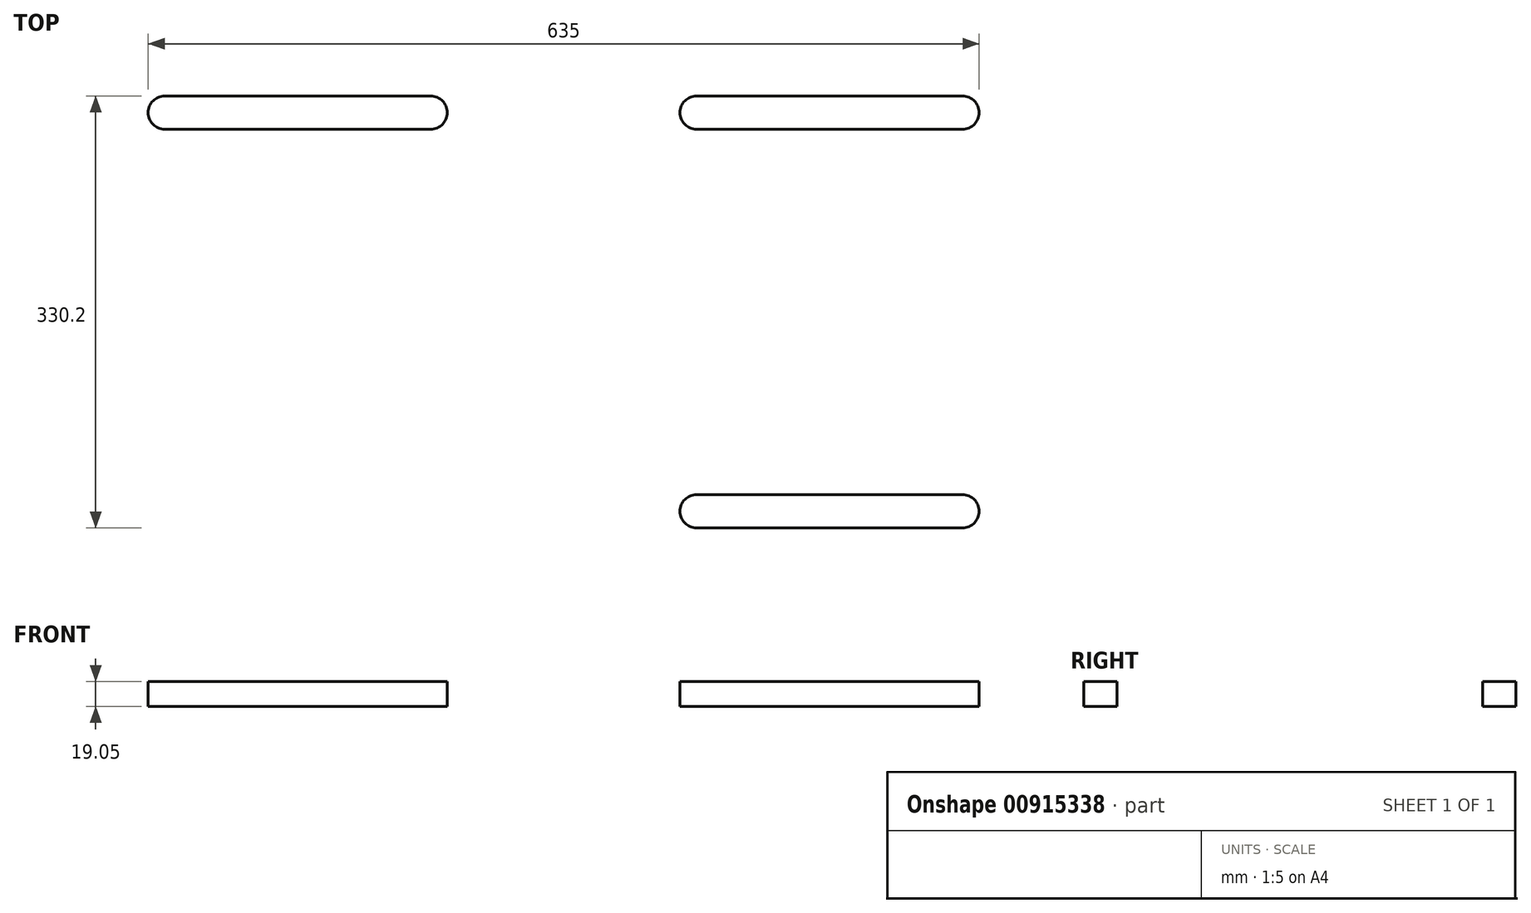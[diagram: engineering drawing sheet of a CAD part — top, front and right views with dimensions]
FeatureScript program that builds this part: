
annotation { "Feature Type Name" : "Feature", "Feature Type Description" : "" }
export const myFeature = defineFeature(function(context is Context, id is Id, definition is map)
    precondition{}
    {
        {
            var Q0;
            Q0=qCreatedBy(makeId("Top.planeOp"),FACE);
            var sketch = newSketch(context, id + "F0", { "sketchPlane" : qUnion([Q0])});
            skLineSegment(sketch, "E0.bottom", {"start": v(0, 0) * mm, "end": v(889, 0) * mm});
            skLineSegment(sketch, "E0.top", {"start": v(0, 596.9) * mm, "end": v(889, 596.9) * mm});
            skLineSegment(sketch, "E0.left", {"start": v(0, 0) * mm, "end": v(0, 596.9) * mm});
            skLineSegment(sketch, "E0.right", {"start": v(889, 0) * mm, "end": v(889, 596.9) * mm});
            skSolve(sketch);
        }
        {
            var Q0;
            Q0 = qSketchRegion(id + "F0", true);
            extrude(context, id + "F1", {"entities" : qUnion([Q0]), "depth" : 19.05 * mm, "offsetDistance" : 25.4 * mm});
        }
        {
            var Q0;
            Q0=makeQuery(id+"F1.opExtrude","CAP_FACE",FACE,{"disambiguationData":[OSD([sQuery(id+"F0.wireOp",EDGE,"E0.bottom"),sQuery(id+"F0.wireOp",EDGE,"E0.top"),sQuery(id+"F0.wireOp",EDGE,"E0.left"),sQuery(id+"F0.wireOp",EDGE,"E0.right")])],"isStart":false});
            var sketch = newSketch(context, id + "F2", { "sketchPlane" : qUnion([Q0])});
            skLineSegment(sketch, "E1", {"start": v(444.5, 596.9) * mm, "end": v(444.5, 0) * mm, "construction": true});
            skLineSegment(sketch, "E2", {"start": v(0, 298.45) * mm, "end": v(889, 298.45) * mm, "construction": true});
            skArc(sketch, "E3", {"start": v(139.7, 311.15) * mm, "mid": v(127, 298.45) * mm, "end": v(139.7, 285.75) * mm});
            skLineSegment(sketch, "E4.0", {"start": v(241.3, 596.9) * mm, "end": v(241.3, 0) * mm, "construction": true});
            skLineSegment(sketch, "E5.0", {"start": v(647.7, 596.9) * mm, "end": v(647.7, 0) * mm, "construction": true});
            skArc(sketch, "E6.MirrorC", {"start": v(342.9, 311.15) * mm, "mid": v(355.6, 298.45) * mm, "end": v(342.9, 285.75) * mm});
            skLineSegment(sketch, "E7", {"start": v(139.7, 285.75) * mm, "end": v(342.9, 285.75) * mm});
            skLineSegment(sketch, "E8", {"start": v(139.7, 311.15) * mm, "end": v(342.9, 311.15) * mm});
            skArc(sketch, "E9.MirrorCS", {"start": v(546.1, 311.15) * mm, "mid": v(533.4, 298.45) * mm, "end": v(546.1, 285.75) * mm});
            skArc(sketch, "E10.MirrorCS", {"start": v(749.3, 311.15) * mm, "mid": v(762, 298.45) * mm, "end": v(749.3, 285.75) * mm});
            skLineSegment(sketch, "E11.MirrorCS", {"start": v(749.3, 311.15) * mm, "end": v(546.1, 311.15) * mm});
            skLineSegment(sketch, "E12.MirrorCS", {"start": v(749.3, 285.75) * mm, "end": v(546.1, 285.75) * mm});
            skLineSegment(sketch, "E13.0.1.0", {"start": v(139.7, 438.15) * mm, "end": v(342.9, 438.15) * mm});
            skArc(sketch, "E13.0.1.1", {"start": v(342.9, 463.55) * mm, "mid": v(355.6, 450.85) * mm, "end": v(342.9, 438.15) * mm});
            skArc(sketch, "E13.0.1.2", {"start": v(749.3, 463.55) * mm, "mid": v(762, 450.85) * mm, "end": v(749.3, 438.15) * mm});
            skArc(sketch, "E13.0.1.3", {"start": v(546.1, 463.55) * mm, "mid": v(533.4, 450.85) * mm, "end": v(546.1, 438.15) * mm});
            skLineSegment(sketch, "E13.0.1.4", {"start": v(749.3, 438.15) * mm, "end": v(546.1, 438.15) * mm});
            skArc(sketch, "E13.0.1.5", {"start": v(139.7, 463.55) * mm, "mid": v(127, 450.85) * mm, "end": v(139.7, 438.15) * mm});
            skLineSegment(sketch, "E13.0.1.6", {"start": v(139.7, 463.55) * mm, "end": v(342.9, 463.55) * mm});
            skLineSegment(sketch, "E13.0.1.7", {"start": v(749.3, 463.55) * mm, "end": v(546.1, 463.55) * mm});
            skArc(sketch, "E13.0.1.8", {"start": v(139.7, 463.55) * mm, "mid": v(127, 450.85) * mm, "end": v(139.7, 438.15) * mm});
            skLineSegment(sketch, "E13.0.1.9", {"start": v(749.3, 463.55) * mm, "end": v(546.1, 463.55) * mm});
            skLineSegment(sketch, "E13.0.1.10", {"start": v(139.7, 463.55) * mm, "end": v(342.9, 463.55) * mm});
            skArc(sketch, "E13.0.1.11", {"start": v(749.3, 463.55) * mm, "mid": v(762, 450.85) * mm, "end": v(749.3, 438.15) * mm});
            skLineSegment(sketch, "E13.0.1.12", {"start": v(139.7, 438.15) * mm, "end": v(342.9, 438.15) * mm});
            skLineSegment(sketch, "E13.0.1.13", {"start": v(749.3, 438.15) * mm, "end": v(546.1, 438.15) * mm});
            skArc(sketch, "E13.0.1.14", {"start": v(546.1, 463.55) * mm, "mid": v(533.4, 450.85) * mm, "end": v(546.1, 438.15) * mm});
            skArc(sketch, "E13.0.1.15", {"start": v(342.9, 463.55) * mm, "mid": v(355.6, 450.85) * mm, "end": v(342.9, 438.15) * mm});
            skArc(sketch, "E13.0.1.16", {"start": v(749.3, 463.55) * mm, "mid": v(762, 450.85) * mm, "end": v(749.3, 438.15) * mm});
            skArc(sketch, "E13.0.1.17", {"start": v(546.1, 463.55) * mm, "mid": v(533.4, 450.85) * mm, "end": v(546.1, 438.15) * mm});
            skLineSegment(sketch, "E13.0.1.18", {"start": v(749.3, 438.15) * mm, "end": v(546.1, 438.15) * mm});
            skLineSegment(sketch, "E13.0.1.19", {"start": v(749.3, 463.55) * mm, "end": v(546.1, 463.55) * mm});
            skArc(sketch, "E13.0.1.20", {"start": v(546.1, 463.55) * mm, "mid": v(533.4, 450.85) * mm, "end": v(546.1, 438.15) * mm});
            skLineSegment(sketch, "E13.0.1.21", {"start": v(749.3, 438.15) * mm, "end": v(546.1, 438.15) * mm});
            skLineSegment(sketch, "E13.0.1.22", {"start": v(749.3, 463.55) * mm, "end": v(546.1, 463.55) * mm});
            skArc(sketch, "E13.0.1.23", {"start": v(749.3, 463.55) * mm, "mid": v(762, 450.85) * mm, "end": v(749.3, 438.15) * mm});
            skLineSegment(sketch, "E13.direction1", {"start": v(139.7, 285.75) * mm, "end": v(165.1, 285.75) * mm, "construction": true});
            skLineSegment(sketch, "E13.direction2", {"start": v(139.7, 285.75) * mm, "end": v(139.7, 438.15) * mm, "construction": true});
            skArc(sketch, "E14.MirrorCS", {"start": v(546.1, 133.35) * mm, "mid": v(533.4, 146.05) * mm, "end": v(546.1, 158.75) * mm});
            skLineSegment(sketch, "E15.MirrorCS", {"start": v(749.3, 158.75) * mm, "end": v(546.1, 158.75) * mm});
            skArc(sketch, "E16.MirrorCS", {"start": v(749.3, 133.35) * mm, "mid": v(762, 146.05) * mm, "end": v(749.3, 158.75) * mm});
            skLineSegment(sketch, "E17.MirrorCS", {"start": v(749.3, 133.35) * mm, "end": v(546.1, 133.35) * mm});
            skArc(sketch, "E18.MirrorCS", {"start": v(342.9, 133.35) * mm, "mid": v(355.6, 146.05) * mm, "end": v(342.9, 158.75) * mm});
            skLineSegment(sketch, "E19.MirrorCS", {"start": v(139.7, 133.35) * mm, "end": v(342.9, 133.35) * mm});
            skArc(sketch, "E20.MirrorCS", {"start": v(139.7, 133.35) * mm, "mid": v(127, 146.05) * mm, "end": v(139.7, 158.75) * mm});
            skLineSegment(sketch, "E21.MirrorCS", {"start": v(139.7, 158.75) * mm, "end": v(342.9, 158.75) * mm});
            skSolve(sketch);
        }
        {
            var Q0;
            Q0=makeQuery(id+"F2.imprint","IMPRINT",FACE,{"disambiguationData":[TD([[makeQuery(id+"F2.imprint","IMPRINT",EDGE,{"derivedFrom":sQuery(id+"F2.wireOp",EDGE,"E8")}),1.0]])]});
            var sketch = newSketch(context, id + "F3", { "sketchPlane" : qUnion([Q0])});
            skCircle(sketch, "E22", {"center": v(38.1, 558.8) * mm, "radius": 12.7 * mm});
            skCircle(sketch, "E23.1.0.0", {"center": v(139.7, 558.8) * mm, "radius": 12.7 * mm});
            skCircle(sketch, "E23.2.0.0", {"center": v(241.3, 558.8) * mm, "radius": 12.7 * mm});
            skCircle(sketch, "E23.3.0.0", {"center": v(342.9, 558.8) * mm, "radius": 12.7 * mm});
            skCircle(sketch, "E23.4.0.0", {"center": v(444.5, 558.8) * mm, "radius": 12.7 * mm});
            skCircle(sketch, "E23.5.0.0", {"center": v(546.1, 558.8) * mm, "radius": 12.7 * mm});
            skCircle(sketch, "E23.6.0.0", {"center": v(647.7, 558.8) * mm, "radius": 12.7 * mm});
            skCircle(sketch, "E23.7.0.0", {"center": v(749.3, 558.8) * mm, "radius": 12.7 * mm});
            skCircle(sketch, "E23.8.0.0", {"center": v(850.9, 558.8) * mm, "radius": 12.7 * mm});
            skLineSegment(sketch, "E23.direction1", {"start": v(38.1, 558.8) * mm, "end": v(139.7, 558.8) * mm, "construction": true});
            skCircle(sketch, "E24.MirrorC", {"center": v(342.9, 38.1) * mm, "radius": 12.7 * mm});
            skCircle(sketch, "E25.MirrorC", {"center": v(850.9, 38.1) * mm, "radius": 12.7 * mm});
            skCircle(sketch, "E26.MirrorC", {"center": v(139.7, 38.1) * mm, "radius": 12.7 * mm});
            skCircle(sketch, "E27.MirrorC", {"center": v(241.3, 38.1) * mm, "radius": 12.7 * mm});
            skCircle(sketch, "E28.MirrorC", {"center": v(647.7, 38.1) * mm, "radius": 12.7 * mm});
            skCircle(sketch, "E29.MirrorC", {"center": v(749.3, 38.1) * mm, "radius": 12.7 * mm});
            skCircle(sketch, "E30.MirrorC", {"center": v(38.1, 38.1) * mm, "radius": 12.7 * mm});
            skCircle(sketch, "E31.MirrorC", {"center": v(444.5, 38.1) * mm, "radius": 12.7 * mm});
            skCircle(sketch, "E32.MirrorC", {"center": v(546.1, 38.1) * mm, "radius": 12.7 * mm});
            skLineSegment(sketch, "E33.MirrorCS", {"start": v(38.1, 38.1) * mm, "end": v(139.7, 38.1) * mm, "construction": true});
            skCircle(sketch, "E34.0.1.0", {"center": v(38.1, 457.2) * mm, "radius": 12.7 * mm});
            skCircle(sketch, "E34.0.1.1", {"center": v(38.1, 457.2) * mm, "radius": 12.7 * mm});
            skCircle(sketch, "E34.0.2.0", {"center": v(38.1, 355.6) * mm, "radius": 12.7 * mm});
            skCircle(sketch, "E34.0.2.1", {"center": v(38.1, 355.6) * mm, "radius": 12.7 * mm});
            skCircle(sketch, "E34.0.3.0", {"center": v(38.1, 254) * mm, "radius": 12.7 * mm});
            skCircle(sketch, "E34.0.3.1", {"center": v(38.1, 254) * mm, "radius": 12.7 * mm});
            skCircle(sketch, "E34.0.4.0", {"center": v(38.1, 152.4) * mm, "radius": 12.7 * mm});
            skCircle(sketch, "E34.0.4.1", {"center": v(38.1, 152.4) * mm, "radius": 12.7 * mm});
            skLineSegment(sketch, "E34.direction1", {"start": v(38.1, 558.8) * mm, "end": v(63.5, 558.8) * mm, "construction": true});
            skLineSegment(sketch, "E34.direction2", {"start": v(38.1, 558.8) * mm, "end": v(38.1, 457.2) * mm, "construction": true});
            skCircle(sketch, "E35.MirrorC", {"center": v(850.9, 152.4) * mm, "radius": 12.7 * mm});
            skCircle(sketch, "E36.MirrorC", {"center": v(850.9, 254) * mm, "radius": 12.7 * mm});
            skCircle(sketch, "E37.MirrorC", {"center": v(850.9, 355.6) * mm, "radius": 12.7 * mm});
            skCircle(sketch, "E38.MirrorC", {"center": v(850.9, 457.2) * mm, "radius": 12.7 * mm});
            skSolve(sketch);
        }
        {
            var Q0;
            Q0 = qSketchRegion(id + "F3", true);
            extrude(context, id + "F4", {"entities" : qUnion([Q0]), "operationType" : NewBodyOperationType.REMOVE, "oppositeDirection" : true, "depth" : 25.4 * mm, "offsetDistance" : 25.4 * mm});
        }
        {
            var Q0;
            Q0=makeQuery(id+"F2.imprint","IMPRINT",FACE,{"disambiguationData":[TD([[makeQuery(id+"F2.imprint","IMPRINT",EDGE,{"derivedFrom":sQuery(id+"F2.wireOp",EDGE,"E13.0.1.8")}),1.0]])]});
            var Q1;
            Q1=makeQuery(id+"F2.imprint","IMPRINT",FACE,{"disambiguationData":[TD([[makeQuery(id+"F2.imprint","IMPRINT",EDGE,{"derivedFrom":sQuery(id+"F2.wireOp",EDGE,"E13.0.1.20")}),1.0]])]});
            var Q2;
            Q2=makeQuery(id+"F2.imprint","IMPRINT",FACE,{"disambiguationData":[TD([[makeQuery(id+"F2.imprint","IMPRINT",EDGE,{"derivedFrom":sQuery(id+"F2.wireOp",EDGE,"E8")}),-1.0]])]});
            var Q3;
            Q3=makeQuery(id+"F2.imprint","IMPRINT",FACE,{"disambiguationData":[TD([[makeQuery(id+"F2.imprint","IMPRINT",EDGE,{"derivedFrom":sQuery(id+"F2.wireOp",EDGE,"E12.MirrorCS")}),-1.0]])]});
            var Q4;
            Q4=makeQuery(id+"F2.imprint","IMPRINT",FACE,{"disambiguationData":[TD([[makeQuery(id+"F2.imprint","IMPRINT",EDGE,{"derivedFrom":sQuery(id+"F2.wireOp",EDGE,"E18.MirrorCS")}),1.0]])]});
            var Q5;
            Q5=makeQuery(id+"F2.imprint","IMPRINT",FACE,{"disambiguationData":[TD([[makeQuery(id+"F2.imprint","IMPRINT",EDGE,{"derivedFrom":sQuery(id+"F2.wireOp",EDGE,"E14.MirrorCS")}),-1.0]])]});
            extrude(context, id + "F5", {"entities" : qUnion([Q0, Q1, Q2, Q3, Q4, Q5]), "operationType" : NewBodyOperationType.REMOVE, "oppositeDirection" : true, "depth" : 25.4 * mm, "offsetDistance" : 25.4 * mm});
        }
    });
